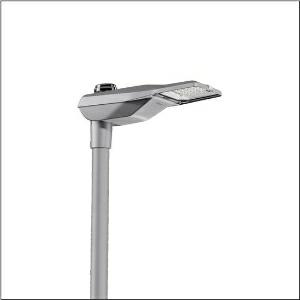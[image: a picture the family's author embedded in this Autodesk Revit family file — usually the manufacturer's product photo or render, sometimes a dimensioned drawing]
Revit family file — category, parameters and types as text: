
# Revit family: streetlight_sl_21_micro___p0_8a_5xe5u57n08db_dcc6
name_source: partatom
category: Lighting Fixtures
units: mm (PartAtom-declared; Revit-internal decimal feet)

## family parameters
Cut with Voids When Loaded = No
Host = Face
Light Source = No
Part Type = Normal
Room Calculation Point = No
Round Connector Dimension = Use Diameter
Shared = No

## types (1)
- --- (1 x LED, 4340 lm, 39.1 W, 3000K)
    Apparent Load = 39 VA
    CIE Flux Codes = 33 69 96 100 100
    Color Rendering = 80
    Color Temperature = 3000K
    Default Elevation = 1800 mm
    Description = Streetlight SL 21 micro, mast luminaire, primary light control with lens, of PMMA, primary optical cover: cover, of toughened safety glass, transparent, light distribution: P0.8a, light emission: direct distribution, primary light characteristic: asymmetric, installation type: post-top, LED, 3G 1.5mm², High Power LED, rated luminous flux: 4.340lm, luminous efficacy: 111lm/W, light colour: 830, colour temperature: 3000K, control gear: NEMA (7pin), control: flexible luminous flux parameterisation, time-dependent luminous flux control, constant luminous flux control, pre-setting: linear dimming characteristic, overheat protection, mains connection: 230..240V, AC, 50/60Hz, connection cable pre-assembled, cable length: 6,5m, wiring characteristics: H07RN-F, start of lifetime: 39W, end of service life: 41W, reduction: 18W, luminaire housing, of diecast aluminium (EN AC-44300), powder-coated, Siteco® metallic grey (DB 702S), corrosivity category C5 mid according to DIN EN ISO 12944, multi-level sealing system, sealing non-destructively replaceable, inclination adjustable: 0°, 5°, 10°, 15°, length: 528mm, width: 235mm, height: 110mm, spigot size: 76/60mm (post-top), mounting height: 4..8m, protection rating (complete): IP66, insulation class (complete): insulation class I (protective earthing), certification: CE, ENEC, ENEC+, VDE, impact resistance: IK10, permissible operating ambient temperature for outdoor applications: -40..+50°C, standard-compliant lighting for roads and squares, packaging unit: 1 piece

Light Distribution: P0.8a
    Height = 110 mm
    Lamp = 1 x LED
    Lamp Light Flux = 4340 lm
    Lamp Power = 39.1 W
    Lamp count = 1
    Length = 528 mm
    Luminous efficacy = 111 lm/W
    Manufacturer = Siteco
    ModVariant = No
    Model = 5XE5U57N08DB
    Number of Poles = 1
    OnlyDefault = Yes
    Power Factor = 1
    Product Name = Streetlight SL 21 micro | P0.8a
    Product group = mast luminaire | pylon top
    ProductGroupID = 6100
    Protection Class = Protection class I
    Protection Degree = IP 66
    RLX_Detail_Level = 1
    RLX_Emergency_Light_Flux = 0 lm
    RLX_Emergency_Type = 0
    RLX_Emergency_Type_DB = No
    RlxData = <blob elided: 99429 chars, md5=97300f60>
    Socket = socket
    Standby Power = 0 W
    System Light Flux = 4340 lm
    System Power = 39 W
    Type Comments = factory setting: luminous flux: 100 % | dim-lin: 254 | 765 mA
    Type Image = l_1294375.jpg
    URL = http://relux.com
    VarID = @adj_073730
    Voltage = 0 V
    Weight = 0.00 kg
    Width = 235 mm

## geometry (parser evidence)
native form markers: Blend x4, Sweep x9
no freeform markers — native parametric forms only
